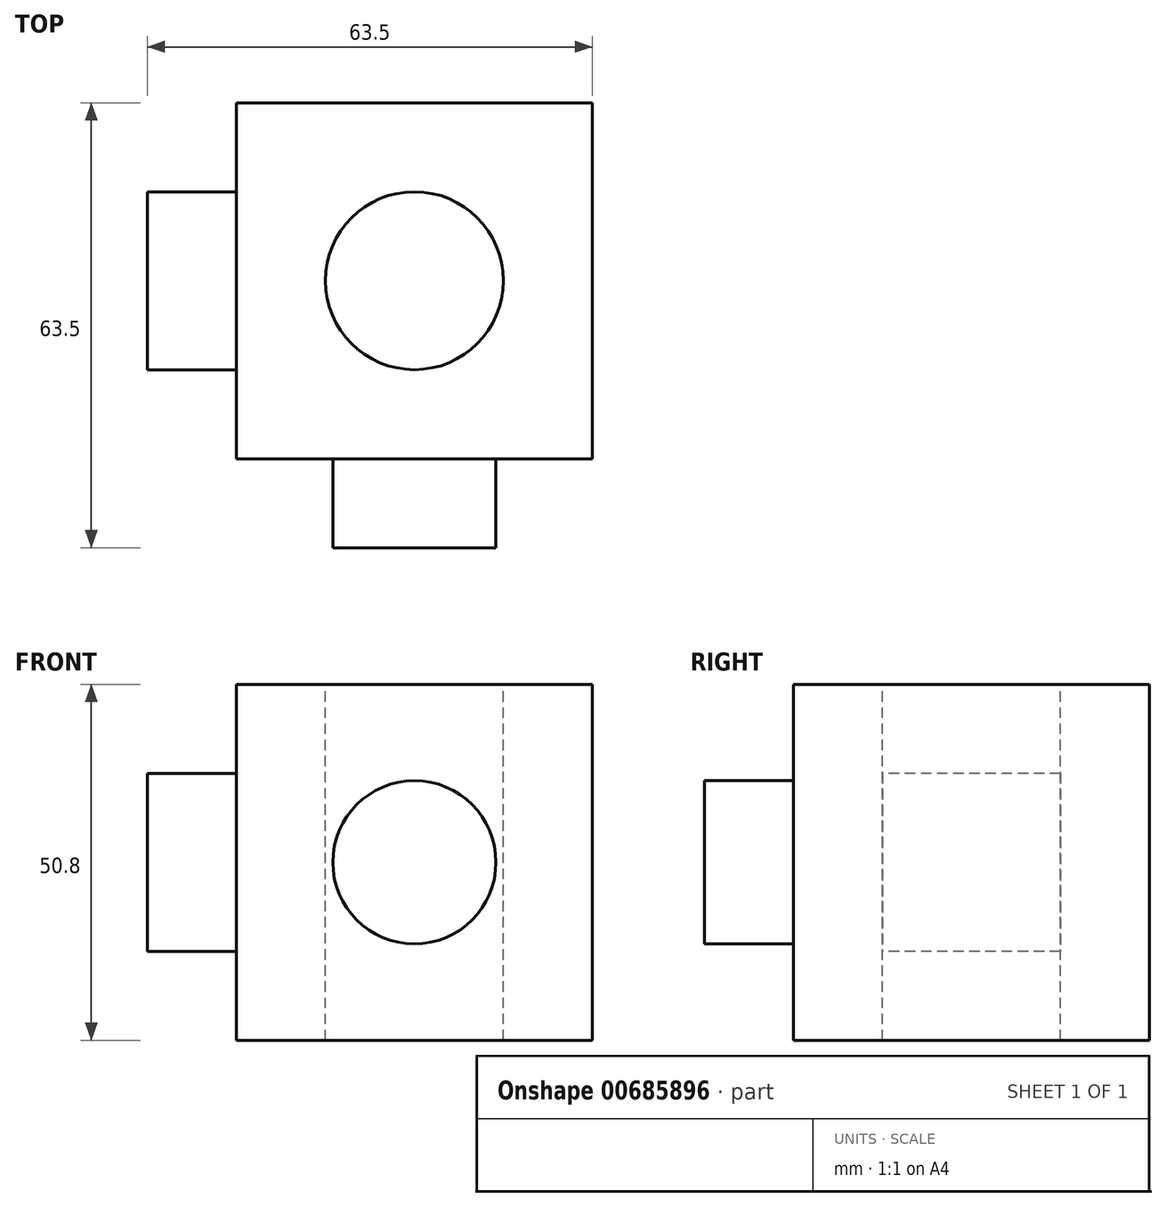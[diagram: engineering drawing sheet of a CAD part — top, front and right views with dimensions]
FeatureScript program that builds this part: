
annotation { "Feature Type Name" : "Feature", "Feature Type Description" : "" }
export const myFeature = defineFeature(function(context is Context, id is Id, definition is map)
    precondition{}
    {
        {
            var Q0;
            Q0=qCreatedBy(makeId("Top.planeOp"),FACE);
            var sketch = newSketch(context, id + "F0", { "sketchPlane" : qUnion([Q0])});
            skLineSegment(sketch, "E0.bottom", {"start": v(-32.56, 69.8) * mm, "end": v(18.24, 69.8) * mm});
            skLineSegment(sketch, "E0.top", {"start": v(-32.56, 19) * mm, "end": v(18.24, 19) * mm});
            skLineSegment(sketch, "E0.left", {"start": v(-32.56, 69.8) * mm, "end": v(-32.56, 19) * mm});
            skLineSegment(sketch, "E0.right", {"start": v(18.24, 69.8) * mm, "end": v(18.24, 19) * mm});
            skSolve(sketch);
        }
        {
            var Q0;
            Q0 = qSketchRegion(id + "F0", true);
            extrude(context, id + "F1", {"entities" : qUnion([Q0]), "depth" : 50.8 * mm, "offsetDistance" : 25.4 * mm});
        }
        {
            var Q0;
            Q0=makeQuery(id+"F1.opExtrude","SWEPT_FACE",FACE,{"disambiguationData":[OSD([sQuery(id+"F0.wireOp",EDGE,"E0.left")])]});
            var sketch = newSketch(context, id + "F2", { "sketchPlane" : qUnion([Q0])});
            skLineSegment(sketch, "E1.bottom", {"start": v(-57.1, 38.1) * mm, "end": v(-31.7, 38.1) * mm});
            skLineSegment(sketch, "E1.top", {"start": v(-57.1, 12.7) * mm, "end": v(-31.7, 12.7) * mm});
            skLineSegment(sketch, "E1.left", {"start": v(-57.1, 38.1) * mm, "end": v(-57.1, 12.7) * mm});
            skLineSegment(sketch, "E1.right", {"start": v(-31.7, 38.1) * mm, "end": v(-31.7, 12.7) * mm});
            skSolve(sketch);
        }
        {
            var Q0;
            Q0 = qSketchRegion(id + "F2", true);
            extrude(context, id + "F3", {"entities" : qUnion([Q0]), "operationType" : NewBodyOperationType.ADD, "depth" : 12.7 * mm, "offsetDistance" : 25.4 * mm});
        }
        {
            var Q0;
            Q0=makeQuery(id+"F1.opExtrude","SWEPT_FACE",FACE,{"disambiguationData":[OSD([sQuery(id+"F0.wireOp",EDGE,"E0.top")])]});
            var sketch = newSketch(context, id + "F4", { "sketchPlane" : qUnion([Q0])});
            skCircle(sketch, "E2", {"center": v(-7.16, 25.4) * mm, "radius": 11.64 * mm});
            skSolve(sketch);
        }
        {
            var Q0;
            Q0 = qSketchRegion(id + "F4", true);
            extrude(context, id + "F5", {"entities" : qUnion([Q0]), "operationType" : NewBodyOperationType.ADD, "depth" : 12.7 * mm, "offsetDistance" : 25.4 * mm});
        }
        {
            var Q0;
            Q0=makeQuery(id+"F1.opExtrude","CAP_FACE",FACE,{"disambiguationData":[OSD([sQuery(id+"F0.wireOp",EDGE,"E0.bottom"),sQuery(id+"F0.wireOp",EDGE,"E0.top"),sQuery(id+"F0.wireOp",EDGE,"E0.left"),sQuery(id+"F0.wireOp",EDGE,"E0.right")])],"isStart":false});
            var sketch = newSketch(context, id + "F6", { "sketchPlane" : qUnion([Q0])});
            skCircle(sketch, "E3", {"center": v(-7.16, 44.4) * mm, "radius": 12.7 * mm});
            skSolve(sketch);
        }
        {
            var Q0;
            Q0 = qSketchRegion(id + "F6", true);
            extrude(context, id + "F7", {"entities" : qUnion([Q0]), "operationType" : NewBodyOperationType.REMOVE, "oppositeDirection" : true, "depth" : 50.8 * mm, "offsetDistance" : 25.4 * mm});
        }
    });
